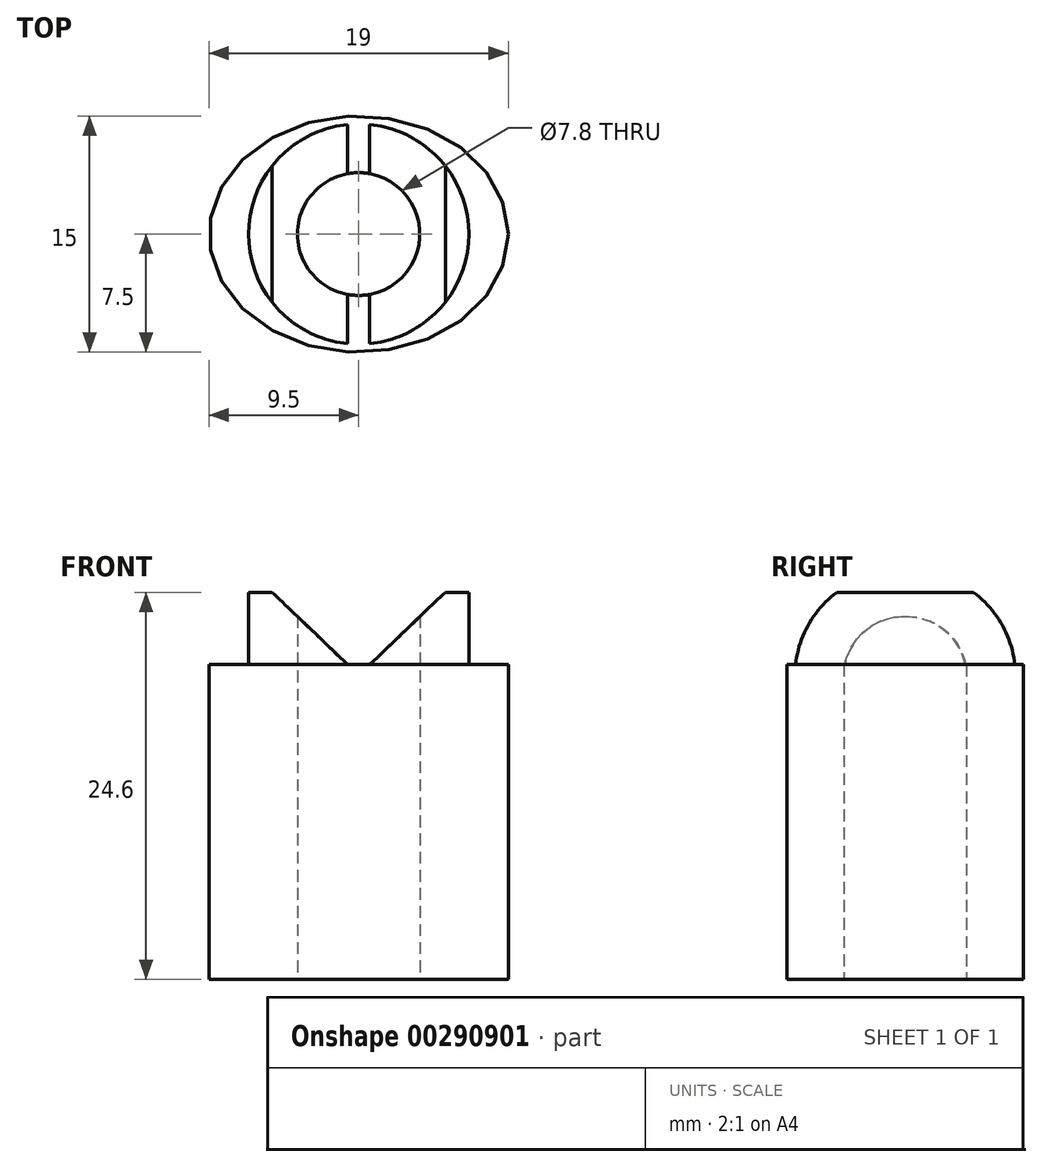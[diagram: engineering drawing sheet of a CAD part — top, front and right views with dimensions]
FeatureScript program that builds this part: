
annotation { "Feature Type Name" : "Feature", "Feature Type Description" : "" }
export const myFeature = defineFeature(function(context is Context, id is Id, definition is map)
    precondition{}
    {
        {
            var Q0;
            Q0=qCreatedBy(makeId("Top.planeOp"),FACE);
            var sketch = newSketch(context, id + "F0", { "sketchPlane" : qUnion([Q0])});
            skEllipse(sketch, "E0", {"center": v(0, 0) * mm, "majorRadius": 9.5 * mm, "minorRadius": 7.5 * mm, "majorAxis": v(1, 0)});
            skSolve(sketch);
        }
        {
            var Q0;
            Q0=makeQuery(id+"F0.imprint","IMPRINT",FACE,{"disambiguationData":[TD([[makeQuery(id+"F0.imprint","IMPRINT",EDGE,{"derivedFrom":sQuery(id+"F0.wireOp",EDGE,"E0")}),1.0]])]});
            extrude(context, id + "F1", {"entities" : qUnion([Q0]), "depth" : 20 * mm});
        }
        {
            var Q0;
            Q0=makeQuery(id+"F1.opExtrude","CAP_FACE",FACE,{"disambiguationData":[OSD([sQuery(id+"F0.wireOp",EDGE,"E0")])],"isStart":false});
            var sketch = newSketch(context, id + "F2", { "sketchPlane" : qUnion([Q0])});
            skCircle(sketch, "E1", {"center": v(0, 0) * mm, "radius": 7 * mm});
            skSolve(sketch);
        }
        {
            var Q0;
            Q0=makeQuery(id+"F2.imprint","IMPRINT",FACE,{"disambiguationData":[TD([[makeQuery(id+"F2.imprint","IMPRINT",EDGE,{"derivedFrom":sQuery(id+"F2.wireOp",EDGE,"E1")}),1.0]])]});
            extrude(context, id + "F3", {"entities" : qUnion([Q0]), "operationType" : NewBodyOperationType.ADD, "depth" : 4.6 * mm});
        }
        {
            var Q0;
            Q0=qCreatedBy(makeId("Front.planeOp"),FACE);
            var sketch = newSketch(context, id + "F4", { "sketchPlane" : qUnion([Q0])});
            skLineSegment(sketch, "E2.bottom", {"start": v(-0.7, 20) * mm, "end": v(0.7, 20) * mm});
            skLineSegment(sketch, "E2.top", {"start": v(-0.7, 24.6) * mm, "end": v(0.7, 24.6) * mm});
            skLineSegment(sketch, "E3.top", {"start": v(-5.5, 24.6) * mm, "end": v(5.5, 24.6) * mm});
            skLineSegment(sketch, "E4", {"start": v(-0.7, 20) * mm, "end": v(-5.5, 24.6) * mm});
            skLineSegment(sketch, "E5", {"start": v(5.5, 24.6) * mm, "end": v(0.7, 20) * mm});
            skSolve(sketch);
        }
        {
            var Q0;
            Q0=qSketchRegion(id+"F4",true);
            extrude(context, id + "F5", {"entities" : qUnion([Q0]), "operationType" : NewBodyOperationType.REMOVE, "endBound" : BoundingType.SYMMETRIC, "depth" : 25 * mm});
        }
        {
            var Q0;
            Q0=makeQuery(id+"F1.opExtrude","CAP_FACE",FACE,{"disambiguationData":[OSD([sQuery(id+"F0.wireOp",EDGE,"E0")])],"isStart":true});
            var sketch = newSketch(context, id + "F6", { "sketchPlane" : qUnion([Q0])});
            skCircle(sketch, "E6", {"center": v(0, 0) * mm, "radius": 3.9 * mm});
            skSolve(sketch);
        }
        {
            var Q0;
            Q0=qSketchRegion(id+"F6",true);
            extrude(context, id + "F7", {"entities" : qUnion([Q0]), "operationType" : NewBodyOperationType.REMOVE, "endBound" : BoundingType.THROUGH_ALL, "oppositeDirection" : true, "depth" : 25 * mm});
        }
    });
